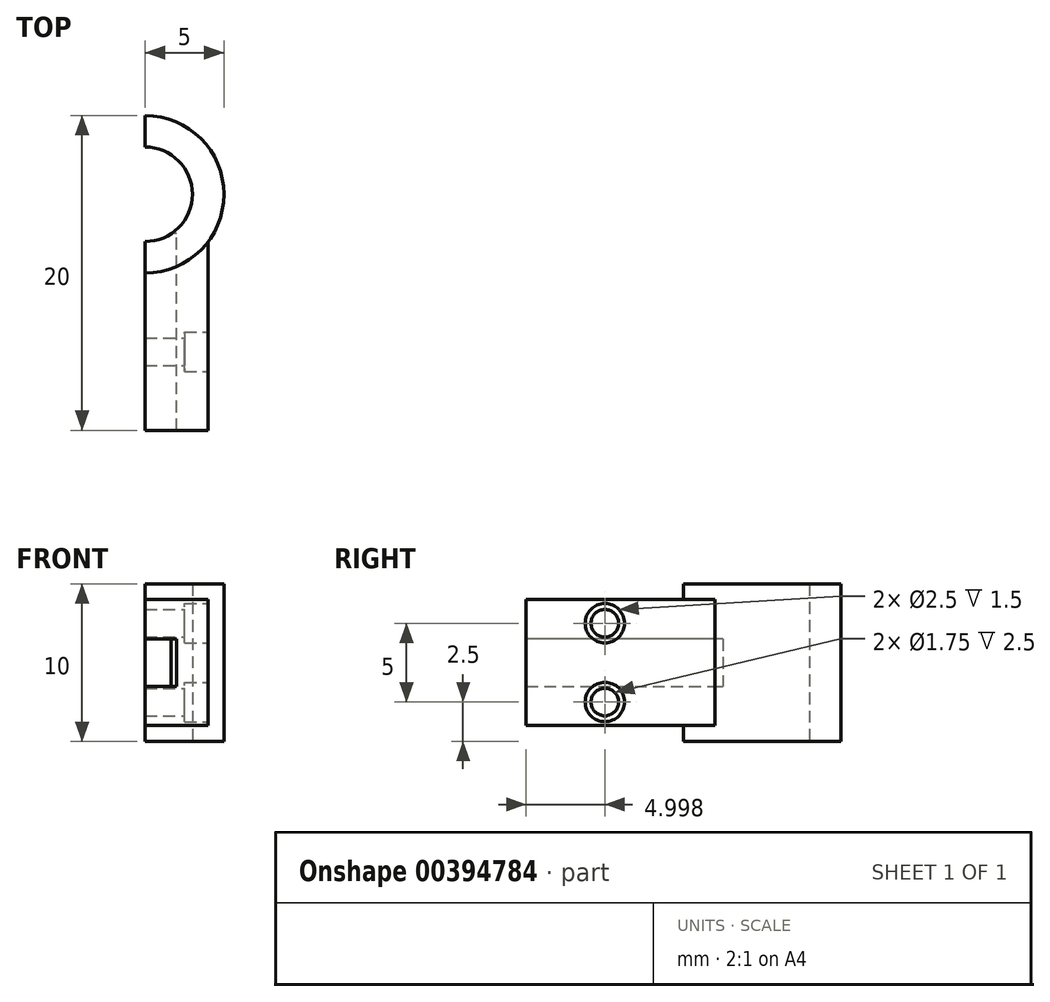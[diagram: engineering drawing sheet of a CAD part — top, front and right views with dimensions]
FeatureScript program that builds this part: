
annotation { "Feature Type Name" : "Feature", "Feature Type Description" : "" }
export const myFeature = defineFeature(function(context is Context, id is Id, definition is map)
    precondition{}
    {
        {
            var Q0;
            Q0=qCreatedBy(makeId("Top.planeOp"),FACE);
            var sketch = newSketch(context, id + "F0", { "sketchPlane" : qUnion([Q0])});
            skLineSegment(sketch, "E0", {"start": v(1.47, 23.22) * mm, "end": v(1.47, 35.22) * mm});
            skArc(sketch, "E1", {"start": v(-2.53, 35.22) * mm, "mid": v(0.47, 38.22) * mm, "end": v(-2.53, 41.22) * mm});
            skArc(sketch, "E2", {"start": v(-2.53, 33.22) * mm, "mid": v(2.47, 38.22) * mm, "end": v(-2.53, 43.22) * mm});
            skPoint(sketch, "E3.orphan", {"position": v(1.47, 24.21) * mm});
            skLineSegment(sketch, "E4", {"start": v(-2.53, 43.22) * mm, "end": v(-2.53, 23.22) * mm});
            skLineSegment(sketch, "E5", {"start": v(1.47, 23.22) * mm, "end": v(-2.53, 23.22) * mm});
            skSolve(sketch);
        }
        {
            var Q0;
            {var subQ0=sQuery(id+"F0.wireOp",EDGE,"E0");Q0=makeQuery(id+"F0.imprint","IMPRINT",FACE,{"disambiguationData":[TD([[makeQuery(id+"F0.imprint","IMPRINT",EDGE,{"derivedFrom":subQ0}),1.0]])]});}
            extrude(context, id + "F1", {"entities" : qUnion([Q0]), "endBound" : BoundingType.SYMMETRIC, "depth" : 8 * mm});
        }
        {
            var Q0;
            {var subQ1=sQuery(id+"F0.wireOp",EDGE,"E1");Q0=makeQuery(id+"F0.imprint","IMPRINT",FACE,{"disambiguationData":[TD([[makeQuery(id+"F0.imprint","IMPRINT",EDGE,{"derivedFrom":subQ1}),-1.0]])]});}
            extrude(context, id + "F2", {"entities" : qUnion([Q0]), "operationType" : NewBodyOperationType.ADD, "endBound" : BoundingType.SYMMETRIC, "depth" : 10 * mm});
        }
        {
            var Q0;
            {var subQ0=sQuery(id+"F0.wireOp",EDGE,"E4");Q0=makeQuery(id+"F2.boolean.opBoolean","MERGE",FACE,{"derivedFrom":[makeQuery(id+"F1.opExtrude","SWEPT_FACE",FACE,{"disambiguationData":[OSD([subQ0])]}),makeQuery(id+"F2.opExtrude","SWEPT_FACE",FACE,{"disambiguationData":[OSD([subQ0]),TDD([makeQuery(id+"F0.imprint","IMPRINT",EDGE,{"disambiguationData":[TD([[makeQuery(id+"F0.imprint","INTERSECT",VERTEX,{"disambiguationData":[OD(0.0)],"derivedFrom":[sQuery(id+"F0.wireOp",EDGE,"E1"),subQ0]}),-1.0]])],"derivedFrom":subQ0})])]})]});}
            var sketch = newSketch(context, id + "F3", { "sketchPlane" : qUnion([Q0])});
            skLineSegment(sketch, "E6", {"start": v(-23.22, -1.5) * mm, "end": v(-35.71, -1.5) * mm});
            skLineSegment(sketch, "E7", {"start": v(-35.71, -1.5) * mm, "end": v(-35.71, 1.5) * mm});
            skLineSegment(sketch, "E8", {"start": v(-35.71, 1.5) * mm, "end": v(-23.22, 1.5) * mm});
            skLineSegment(sketch, "E9", {"start": v(-23.22, 1.5) * mm, "end": v(-23.22, -1.5) * mm});
            skSolve(sketch);
        }
        {
            var Q0;
            {var subQ0=sQuery(id+"F3.wireOp",EDGE,"E9");Q0=makeQuery(id+"F3.imprint","IMPRINT",FACE,{"disambiguationData":[TD([[makeQuery(id+"F3.imprint","IMPRINT",EDGE,{"derivedFrom":subQ0}),-1.0]])]});}
            var Q1;
            {var subQ0=sQuery(id+"F3.wireOp",EDGE,"E7");Q1=makeQuery(id+"F3.imprint","IMPRINT",FACE,{"disambiguationData":[TD([[makeQuery(id+"F3.imprint","IMPRINT",EDGE,{"derivedFrom":subQ0}),-1.0]])]});}
            extrude(context, id + "F4", {"entities" : qUnion([Q0, Q1]), "operationType" : NewBodyOperationType.REMOVE, "oppositeDirection" : true, "depth" : 2 * mm});
        }
        {
            var Q0;
            Q0=makeQuery(id+"F1.opExtrude","SWEPT_FACE",FACE,{"disambiguationData":[OSD([sQuery(id+"F0.wireOp",EDGE,"E0")])]});
            var sketch = newSketch(context, id + "F5", { "sketchPlane" : qUnion([Q0])});
            skCircle(sketch, "E10", {"center": v(28.22, 2.5) * mm, "radius": 1.25 * mm});
            skCircle(sketch, "E11", {"center": v(28.22, -2.5) * mm, "radius": 1.25 * mm});
            skCircle(sketch, "E12", {"center": v(28.22, 2.5) * mm, "radius": 0.88 * mm});
            skCircle(sketch, "E13", {"center": v(28.22, -2.5) * mm, "radius": 0.88 * mm});
            skSolve(sketch);
        }
        {
            var Q0;
            Q0=makeQuery(id+"F5.imprint","IMPRINT",FACE,{"disambiguationData":[TD([[makeQuery(id+"F5.imprint","IMPRINT",EDGE,{"derivedFrom":sQuery(id+"F5.wireOp",EDGE,"E10")}),1.0]])]});
            var Q1;
            Q1=makeQuery(id+"F5.imprint","IMPRINT",FACE,{"disambiguationData":[TD([[makeQuery(id+"F5.imprint","IMPRINT",EDGE,{"derivedFrom":sQuery(id+"F5.wireOp",EDGE,"E11")}),1.0]])]});
            extrude(context, id + "F6", {"entities" : qUnion([Q0, Q1]), "operationType" : NewBodyOperationType.REMOVE, "oppositeDirection" : true, "depth" : 1.5 * mm});
        }
        {
            var Q0;
            Q0=makeQuery(id+"F6.boolean.opBoolean","SPLIT",FACE,{"disambiguationData":[TD([makeQuery(id+"F6.opExtrude","SWEPT_FACE",FACE,{"disambiguationData":[OSD([sQuery(id+"F5.wireOp",EDGE,"E12")])]})])],"derivedFrom":makeQuery(id+"F1.opExtrude","SWEPT_FACE",FACE,{"disambiguationData":[OSD([sQuery(id+"F0.wireOp",EDGE,"E0")])]})});
            var Q1;
            Q1=makeQuery(id+"F6.boolean.opBoolean","SPLIT",FACE,{"disambiguationData":[TD([makeQuery(id+"F6.opExtrude","SWEPT_FACE",FACE,{"disambiguationData":[OSD([sQuery(id+"F5.wireOp",EDGE,"E13")])]})])],"derivedFrom":makeQuery(id+"F1.opExtrude","SWEPT_FACE",FACE,{"disambiguationData":[OSD([sQuery(id+"F0.wireOp",EDGE,"E0")])]})});
            extrude(context, id + "F7", {"entities" : qUnion([Q0, Q1]), "operationType" : NewBodyOperationType.REMOVE, "oppositeDirection" : true, "depth" : 25 * mm});
        }
    });
